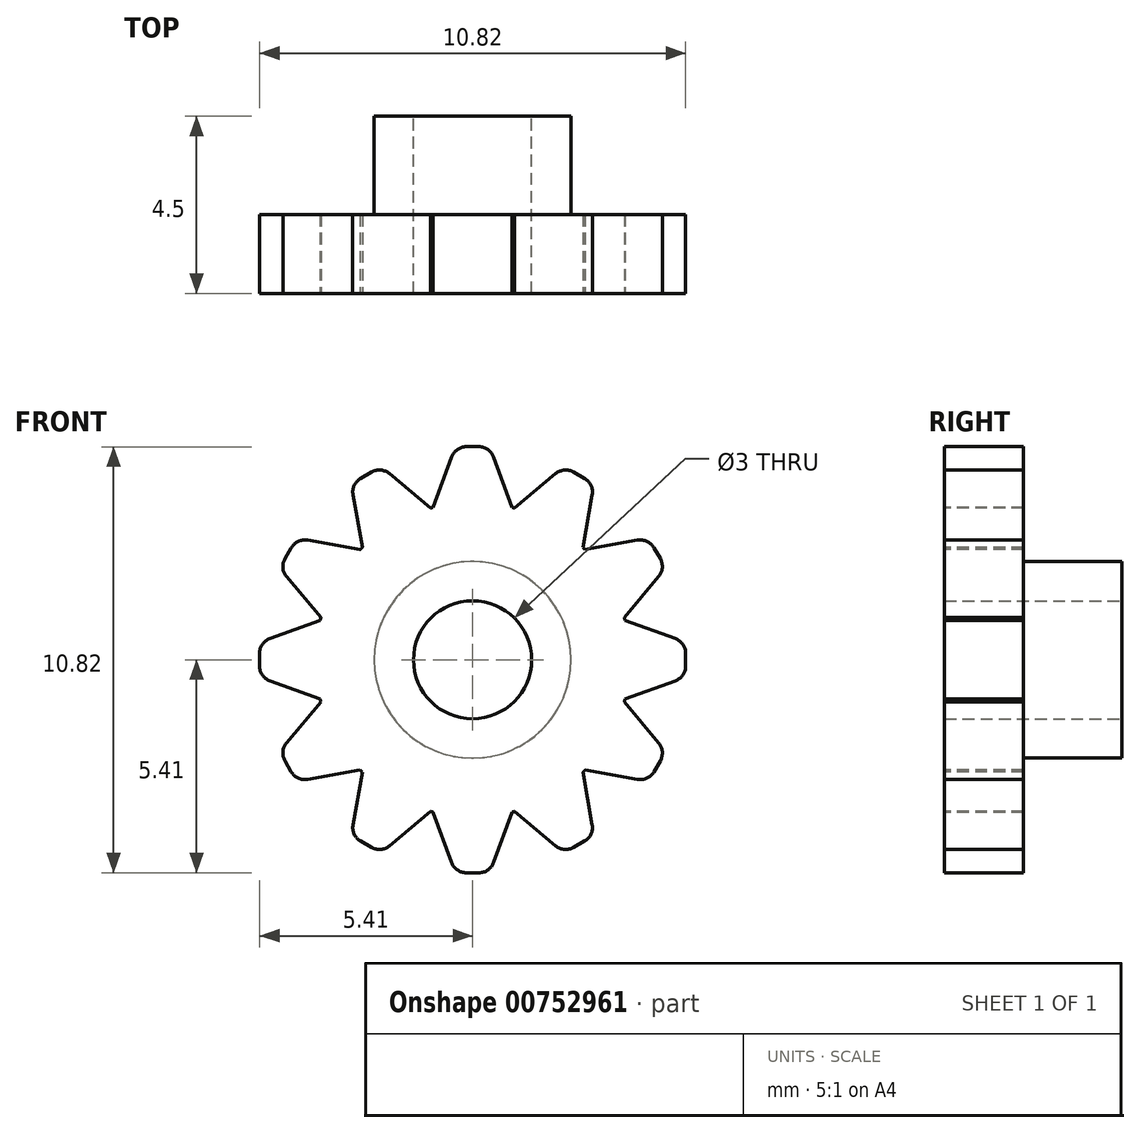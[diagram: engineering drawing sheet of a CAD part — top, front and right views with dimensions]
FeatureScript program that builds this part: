
annotation { "Feature Type Name" : "Feature", "Feature Type Description" : "" }
export const myFeature = defineFeature(function(context is Context, id is Id, definition is map)
    precondition{}
    {
        {
            var Q0;
            Q0=qCreatedBy(makeId("Front.planeOp"),FACE);
            var sketch = newSketch(context, id + "F0", { "sketchPlane" : qUnion([Q0])});
            skCircle(sketch, "E0", {"center": v(0, 0) * mm, "radius": 4 * mm});
            skCircle(sketch, "E1", {"center": v(0, 0) * mm, "radius": 1.5 * mm});
            skSolve(sketch);
        }
        {
            var Q0;
            Q0 = qSketchRegion(id + "F0", true);
            extrude(context, id + "F1", {"entities" : qUnion([Q0]), "depth" : 2 * mm, "offsetDistance" : 25 * mm});
        }
        {
            var Q0;
            Q0=makeQuery(id+"F1.opExtrude","CAP_FACE",FACE,{"disambiguationData":[OSD([sQuery(id+"F0.wireOp",EDGE,"E0")])],"isStart":false});
            var sketch = newSketch(context, id + "F2", { "sketchPlane" : qUnion([Q0])});
            skLineSegment(sketch, "E2", {"start": v(0, 0) * mm, "end": v(0, 7.76) * mm, "construction": true});
            skLineSegment(sketch, "E3", {"start": v(0, 5.41) * mm, "end": v(0.44, 5.41) * mm});
            skLineSegment(sketch, "E4", {"start": v(0.44, 5.41) * mm, "end": v(1, 3.87) * mm});
            skLineSegment(sketch, "E5.MirrorCS", {"start": v(0, 5.41) * mm, "end": v(-0.44, 5.41) * mm});
            skLineSegment(sketch, "E6.MirrorCS", {"start": v(-0.44, 5.41) * mm, "end": v(-1, 3.87) * mm});
            skLineSegment(sketch, "E7", {"start": v(-1, 3.87) * mm, "end": v(1, 3.87) * mm});
            skLineSegment(sketch, "E8.1.0", {"start": v(-2.8, 2.85) * mm, "end": v(-1.07, 3.85) * mm});
            skLineSegment(sketch, "E8.1.1", {"start": v(-3.09, 4.47) * mm, "end": v(-2.8, 2.85) * mm});
            skLineSegment(sketch, "E8.1.2", {"start": v(-2.33, 4.9) * mm, "end": v(-1.07, 3.85) * mm});
            skLineSegment(sketch, "E8.1.3", {"start": v(-2.7, 4.69) * mm, "end": v(-2.33, 4.9) * mm});
            skLineSegment(sketch, "E8.1.4", {"start": v(-2.7, 4.69) * mm, "end": v(-3.09, 4.47) * mm});
            skLineSegment(sketch, "E8.2.0", {"start": v(-3.85, 1.07) * mm, "end": v(-2.85, 2.8) * mm});
            skLineSegment(sketch, "E8.2.1", {"start": v(-4.9, 2.33) * mm, "end": v(-3.85, 1.07) * mm});
            skLineSegment(sketch, "E8.2.2", {"start": v(-4.47, 3.09) * mm, "end": v(-2.85, 2.8) * mm});
            skLineSegment(sketch, "E8.2.3", {"start": v(-4.69, 2.7) * mm, "end": v(-4.47, 3.09) * mm});
            skLineSegment(sketch, "E8.2.4", {"start": v(-4.69, 2.7) * mm, "end": v(-4.9, 2.33) * mm});
            skLineSegment(sketch, "E8.3.0", {"start": v(-3.87, -1) * mm, "end": v(-3.87, 1) * mm});
            skLineSegment(sketch, "E8.3.1", {"start": v(-5.41, -0.44) * mm, "end": v(-3.87, -1) * mm});
            skLineSegment(sketch, "E8.3.2", {"start": v(-5.41, 0.44) * mm, "end": v(-3.87, 1) * mm});
            skLineSegment(sketch, "E8.3.3", {"start": v(-5.41, 0) * mm, "end": v(-5.41, 0.44) * mm});
            skLineSegment(sketch, "E8.3.4", {"start": v(-5.41, 0) * mm, "end": v(-5.41, -0.44) * mm});
            skLineSegment(sketch, "E8.4.0", {"start": v(-2.85, -2.8) * mm, "end": v(-3.85, -1.07) * mm});
            skLineSegment(sketch, "E8.4.1", {"start": v(-4.47, -3.09) * mm, "end": v(-2.85, -2.8) * mm});
            skLineSegment(sketch, "E8.4.2", {"start": v(-4.9, -2.33) * mm, "end": v(-3.85, -1.07) * mm});
            skLineSegment(sketch, "E8.4.3", {"start": v(-4.69, -2.7) * mm, "end": v(-4.9, -2.33) * mm});
            skLineSegment(sketch, "E8.4.4", {"start": v(-4.69, -2.7) * mm, "end": v(-4.47, -3.09) * mm});
            skLineSegment(sketch, "E8.5.0", {"start": v(-1.07, -3.85) * mm, "end": v(-2.8, -2.85) * mm});
            skLineSegment(sketch, "E8.5.1", {"start": v(-2.33, -4.9) * mm, "end": v(-1.07, -3.85) * mm});
            skLineSegment(sketch, "E8.5.2", {"start": v(-3.09, -4.47) * mm, "end": v(-2.8, -2.85) * mm});
            skLineSegment(sketch, "E8.5.3", {"start": v(-2.7, -4.69) * mm, "end": v(-3.09, -4.47) * mm});
            skLineSegment(sketch, "E8.5.4", {"start": v(-2.7, -4.69) * mm, "end": v(-2.33, -4.9) * mm});
            skLineSegment(sketch, "E8.6.0", {"start": v(1, -3.87) * mm, "end": v(-1, -3.87) * mm});
            skLineSegment(sketch, "E8.6.1", {"start": v(0.44, -5.41) * mm, "end": v(1, -3.87) * mm});
            skLineSegment(sketch, "E8.6.2", {"start": v(-0.44, -5.41) * mm, "end": v(-1, -3.87) * mm});
            skLineSegment(sketch, "E8.6.3", {"start": v(0, -5.41) * mm, "end": v(-0.44, -5.41) * mm});
            skLineSegment(sketch, "E8.6.4", {"start": v(0, -5.41) * mm, "end": v(0.44, -5.41) * mm});
            skLineSegment(sketch, "E8.7.0", {"start": v(2.8, -2.85) * mm, "end": v(1.07, -3.85) * mm});
            skLineSegment(sketch, "E8.7.1", {"start": v(3.09, -4.47) * mm, "end": v(2.8, -2.85) * mm});
            skLineSegment(sketch, "E8.7.2", {"start": v(2.33, -4.9) * mm, "end": v(1.07, -3.85) * mm});
            skLineSegment(sketch, "E8.7.3", {"start": v(2.7, -4.69) * mm, "end": v(2.33, -4.9) * mm});
            skLineSegment(sketch, "E8.7.4", {"start": v(2.7, -4.69) * mm, "end": v(3.09, -4.47) * mm});
            skLineSegment(sketch, "E8.8.0", {"start": v(3.85, -1.07) * mm, "end": v(2.85, -2.8) * mm});
            skLineSegment(sketch, "E8.8.1", {"start": v(4.9, -2.33) * mm, "end": v(3.85, -1.07) * mm});
            skLineSegment(sketch, "E8.8.2", {"start": v(4.47, -3.09) * mm, "end": v(2.85, -2.8) * mm});
            skLineSegment(sketch, "E8.8.3", {"start": v(4.69, -2.7) * mm, "end": v(4.47, -3.09) * mm});
            skLineSegment(sketch, "E8.8.4", {"start": v(4.69, -2.7) * mm, "end": v(4.9, -2.33) * mm});
            skLineSegment(sketch, "E8.9.0", {"start": v(3.87, 1) * mm, "end": v(3.87, -1) * mm});
            skLineSegment(sketch, "E8.9.1", {"start": v(5.41, 0.44) * mm, "end": v(3.87, 1) * mm});
            skLineSegment(sketch, "E8.9.2", {"start": v(5.41, -0.44) * mm, "end": v(3.87, -1) * mm});
            skLineSegment(sketch, "E8.9.3", {"start": v(5.41, 0) * mm, "end": v(5.41, -0.44) * mm});
            skLineSegment(sketch, "E8.9.4", {"start": v(5.41, 0) * mm, "end": v(5.41, 0.44) * mm});
            skLineSegment(sketch, "E8.10.0", {"start": v(2.85, 2.8) * mm, "end": v(3.85, 1.07) * mm});
            skLineSegment(sketch, "E8.10.1", {"start": v(4.47, 3.09) * mm, "end": v(2.85, 2.8) * mm});
            skLineSegment(sketch, "E8.10.2", {"start": v(4.9, 2.33) * mm, "end": v(3.85, 1.07) * mm});
            skLineSegment(sketch, "E8.10.3", {"start": v(4.69, 2.7) * mm, "end": v(4.9, 2.33) * mm});
            skLineSegment(sketch, "E8.10.4", {"start": v(4.69, 2.7) * mm, "end": v(4.47, 3.09) * mm});
            skLineSegment(sketch, "E8.11.0", {"start": v(1.07, 3.85) * mm, "end": v(2.8, 2.85) * mm});
            skLineSegment(sketch, "E8.11.1", {"start": v(2.33, 4.9) * mm, "end": v(1.07, 3.85) * mm});
            skLineSegment(sketch, "E8.11.2", {"start": v(3.09, 4.47) * mm, "end": v(2.8, 2.85) * mm});
            skLineSegment(sketch, "E8.11.3", {"start": v(2.7, 4.69) * mm, "end": v(3.09, 4.47) * mm});
            skLineSegment(sketch, "E8.11.4", {"start": v(2.7, 4.69) * mm, "end": v(2.33, 4.9) * mm});
            skPoint(sketch, "E8.center", {"position": v(0, 0) * mm});
            skSolve(sketch);
        }
        {
            var Q0;
            Q0 = qSketchRegion(id + "F2", true);
            var Q1;
            Q1=makeQuery(id+"F1.opExtrude","CAP_FACE",FACE,{"disambiguationData":[OSD([sQuery(id+"F0.wireOp",EDGE,"E0"),sQuery(id+"F0.wireOp",EDGE,"E1")])],"isStart":true});
            extrude(context, id + "F3", {"entities" : qUnion([Q0]), "operationType" : NewBodyOperationType.ADD, "endBound" : BoundingType.UP_TO_SURFACE, "oppositeDirection" : true, "depth" : 2 * mm, "endBoundEntityFace" : qUnion([Q1]), "offsetDistance" : 25 * mm});
        }
        {
            var Q0;
            Q0=makeQuery(id+"F3.boolean.opBoolean","MERGE",FACE,{"derivedFrom":[makeQuery(id+"F1.opExtrude","CAP_FACE",FACE,{"disambiguationData":[OSD([sQuery(id+"F0.wireOp",EDGE,"E0"),sQuery(id+"F0.wireOp",EDGE,"E1")])],"isStart":true}),makeQuery(id+"F3.opExtrude","CAP_FACE",FACE,{"disambiguationData":[OSD([sQuery(id+"F2.wireOp",EDGE,"E3"),sQuery(id+"F2.wireOp",EDGE,"E4"),sQuery(id+"F2.wireOp",EDGE,"E5.MirrorCS"),sQuery(id+"F2.wireOp",EDGE,"E6.MirrorCS"),sQuery(id+"F2.wireOp",EDGE,"E7")])],"isStart":false}),makeQuery(id+"F3.opExtrude","CAP_FACE",FACE,{"disambiguationData":[OSD([sQuery(id+"F2.wireOp",EDGE,"E8.1.0"),sQuery(id+"F2.wireOp",EDGE,"E8.1.1"),sQuery(id+"F2.wireOp",EDGE,"E8.1.2"),sQuery(id+"F2.wireOp",EDGE,"E8.1.3"),sQuery(id+"F2.wireOp",EDGE,"E8.1.4")])],"isStart":false}),makeQuery(id+"F3.opExtrude","CAP_FACE",FACE,{"disambiguationData":[OSD([sQuery(id+"F2.wireOp",EDGE,"E8.2.0"),sQuery(id+"F2.wireOp",EDGE,"E8.2.1"),sQuery(id+"F2.wireOp",EDGE,"E8.2.2"),sQuery(id+"F2.wireOp",EDGE,"E8.2.3"),sQuery(id+"F2.wireOp",EDGE,"E8.2.4")])],"isStart":false}),makeQuery(id+"F3.opExtrude","CAP_FACE",FACE,{"disambiguationData":[OSD([sQuery(id+"F2.wireOp",EDGE,"E8.3.0"),sQuery(id+"F2.wireOp",EDGE,"E8.3.1"),sQuery(id+"F2.wireOp",EDGE,"E8.3.2"),sQuery(id+"F2.wireOp",EDGE,"E8.3.3"),sQuery(id+"F2.wireOp",EDGE,"E8.3.4")])],"isStart":false}),makeQuery(id+"F3.opExtrude","CAP_FACE",FACE,{"disambiguationData":[OSD([sQuery(id+"F2.wireOp",EDGE,"E8.4.0"),sQuery(id+"F2.wireOp",EDGE,"E8.4.1"),sQuery(id+"F2.wireOp",EDGE,"E8.4.2"),sQuery(id+"F2.wireOp",EDGE,"E8.4.3"),sQuery(id+"F2.wireOp",EDGE,"E8.4.4")])],"isStart":false}),makeQuery(id+"F3.opExtrude","CAP_FACE",FACE,{"disambiguationData":[OSD([sQuery(id+"F2.wireOp",EDGE,"E8.5.0"),sQuery(id+"F2.wireOp",EDGE,"E8.5.1"),sQuery(id+"F2.wireOp",EDGE,"E8.5.2"),sQuery(id+"F2.wireOp",EDGE,"E8.5.3"),sQuery(id+"F2.wireOp",EDGE,"E8.5.4")])],"isStart":false}),makeQuery(id+"F3.opExtrude","CAP_FACE",FACE,{"disambiguationData":[OSD([sQuery(id+"F2.wireOp",EDGE,"E8.6.0"),sQuery(id+"F2.wireOp",EDGE,"E8.6.1"),sQuery(id+"F2.wireOp",EDGE,"E8.6.2"),sQuery(id+"F2.wireOp",EDGE,"E8.6.3"),sQuery(id+"F2.wireOp",EDGE,"E8.6.4")])],"isStart":false}),makeQuery(id+"F3.opExtrude","CAP_FACE",FACE,{"disambiguationData":[OSD([sQuery(id+"F2.wireOp",EDGE,"E8.7.0"),sQuery(id+"F2.wireOp",EDGE,"E8.7.1"),sQuery(id+"F2.wireOp",EDGE,"E8.7.2"),sQuery(id+"F2.wireOp",EDGE,"E8.7.3"),sQuery(id+"F2.wireOp",EDGE,"E8.7.4")])],"isStart":false}),makeQuery(id+"F3.opExtrude","CAP_FACE",FACE,{"disambiguationData":[OSD([sQuery(id+"F2.wireOp",EDGE,"E8.8.0"),sQuery(id+"F2.wireOp",EDGE,"E8.8.1"),sQuery(id+"F2.wireOp",EDGE,"E8.8.2"),sQuery(id+"F2.wireOp",EDGE,"E8.8.3"),sQuery(id+"F2.wireOp",EDGE,"E8.8.4")])],"isStart":false}),makeQuery(id+"F3.opExtrude","CAP_FACE",FACE,{"disambiguationData":[OSD([sQuery(id+"F2.wireOp",EDGE,"E8.9.0"),sQuery(id+"F2.wireOp",EDGE,"E8.9.1"),sQuery(id+"F2.wireOp",EDGE,"E8.9.2"),sQuery(id+"F2.wireOp",EDGE,"E8.9.3"),sQuery(id+"F2.wireOp",EDGE,"E8.9.4")])],"isStart":false}),makeQuery(id+"F3.opExtrude","CAP_FACE",FACE,{"disambiguationData":[OSD([sQuery(id+"F2.wireOp",EDGE,"E8.10.0"),sQuery(id+"F2.wireOp",EDGE,"E8.10.1"),sQuery(id+"F2.wireOp",EDGE,"E8.10.2"),sQuery(id+"F2.wireOp",EDGE,"E8.10.3"),sQuery(id+"F2.wireOp",EDGE,"E8.10.4")])],"isStart":false}),makeQuery(id+"F3.opExtrude","CAP_FACE",FACE,{"disambiguationData":[OSD([sQuery(id+"F2.wireOp",EDGE,"E8.11.0"),sQuery(id+"F2.wireOp",EDGE,"E8.11.1"),sQuery(id+"F2.wireOp",EDGE,"E8.11.2"),sQuery(id+"F2.wireOp",EDGE,"E8.11.3"),sQuery(id+"F2.wireOp",EDGE,"E8.11.4")])],"isStart":false})]});
            var sketch = newSketch(context, id + "F4", { "sketchPlane" : qUnion([Q0])});
            skCircle(sketch, "E9.0", {"center": v(0, 0) * mm, "radius": 1.5 * mm});
            skCircle(sketch, "E10.0", {"center": v(0, 0) * mm, "radius": 2.5 * mm});
            skSolve(sketch);
        }
        {
            var Q0;
            Q0 = qSketchRegion(id + "F4", true);
            extrude(context, id + "F5", {"entities" : qUnion([Q0]), "operationType" : NewBodyOperationType.ADD, "depth" : 2.5 * mm, "offsetDistance" : 25 * mm});
        }
        {
            var Q0;
            Q0=makeQuery(id+"F3.opExtrude","SWEPT_EDGE",EDGE,{"disambiguationData":[OSD([sQuery(id+"F2.wireOp",EDGE,"E8.11.1"),sQuery(id+"F2.wireOp",EDGE,"E8.11.4")])]});
            var Q1;
            Q1=makeQuery(id+"F3.opExtrude","SWEPT_EDGE",EDGE,{"disambiguationData":[OSD([sQuery(id+"F2.wireOp",EDGE,"E8.11.2"),sQuery(id+"F2.wireOp",EDGE,"E8.11.3")])]});
            var Q2;
            Q2=makeQuery(id+"F3.opExtrude","SWEPT_EDGE",EDGE,{"disambiguationData":[OSD([sQuery(id+"F2.wireOp",EDGE,"E8.10.1"),sQuery(id+"F2.wireOp",EDGE,"E8.10.4")])]});
            var Q3;
            Q3=makeQuery(id+"F3.opExtrude","SWEPT_EDGE",EDGE,{"disambiguationData":[OSD([sQuery(id+"F2.wireOp",EDGE,"E8.10.2"),sQuery(id+"F2.wireOp",EDGE,"E8.10.3")])]});
            var Q4;
            Q4=makeQuery(id+"F3.opExtrude","SWEPT_EDGE",EDGE,{"disambiguationData":[OSD([sQuery(id+"F2.wireOp",EDGE,"E8.9.1"),sQuery(id+"F2.wireOp",EDGE,"E8.9.4")])]});
            var Q5;
            Q5=makeQuery(id+"F3.opExtrude","SWEPT_EDGE",EDGE,{"disambiguationData":[OSD([sQuery(id+"F2.wireOp",EDGE,"E8.9.2"),sQuery(id+"F2.wireOp",EDGE,"E8.9.3")])]});
            var Q6;
            Q6=makeQuery(id+"F3.opExtrude","SWEPT_EDGE",EDGE,{"disambiguationData":[OSD([sQuery(id+"F2.wireOp",EDGE,"E8.8.1"),sQuery(id+"F2.wireOp",EDGE,"E8.8.4")])]});
            var Q7;
            Q7=makeQuery(id+"F3.opExtrude","SWEPT_EDGE",EDGE,{"disambiguationData":[OSD([sQuery(id+"F2.wireOp",EDGE,"E8.8.2"),sQuery(id+"F2.wireOp",EDGE,"E8.8.3")])]});
            var Q8;
            Q8=makeQuery(id+"F3.opExtrude","SWEPT_EDGE",EDGE,{"disambiguationData":[OSD([sQuery(id+"F2.wireOp",EDGE,"E8.7.1"),sQuery(id+"F2.wireOp",EDGE,"E8.7.4")])]});
            var Q9;
            Q9=makeQuery(id+"F3.opExtrude","SWEPT_EDGE",EDGE,{"disambiguationData":[OSD([sQuery(id+"F2.wireOp",EDGE,"E8.7.2"),sQuery(id+"F2.wireOp",EDGE,"E8.7.3")])]});
            var Q10;
            Q10=makeQuery(id+"F3.opExtrude","SWEPT_EDGE",EDGE,{"disambiguationData":[OSD([sQuery(id+"F2.wireOp",EDGE,"E8.6.1"),sQuery(id+"F2.wireOp",EDGE,"E8.6.4")])]});
            var Q11;
            Q11=makeQuery(id+"F3.opExtrude","SWEPT_EDGE",EDGE,{"disambiguationData":[OSD([sQuery(id+"F2.wireOp",EDGE,"E8.6.2"),sQuery(id+"F2.wireOp",EDGE,"E8.6.3")])]});
            var Q12;
            Q12=makeQuery(id+"F3.opExtrude","SWEPT_EDGE",EDGE,{"disambiguationData":[OSD([sQuery(id+"F2.wireOp",EDGE,"E8.5.1"),sQuery(id+"F2.wireOp",EDGE,"E8.5.4")])]});
            var Q13;
            Q13=makeQuery(id+"F3.opExtrude","SWEPT_EDGE",EDGE,{"disambiguationData":[OSD([sQuery(id+"F2.wireOp",EDGE,"E8.5.2"),sQuery(id+"F2.wireOp",EDGE,"E8.5.3")])]});
            var Q14;
            Q14=makeQuery(id+"F3.opExtrude","SWEPT_EDGE",EDGE,{"disambiguationData":[OSD([sQuery(id+"F2.wireOp",EDGE,"E8.4.1"),sQuery(id+"F2.wireOp",EDGE,"E8.4.4")])]});
            var Q15;
            Q15=makeQuery(id+"F3.opExtrude","SWEPT_EDGE",EDGE,{"disambiguationData":[OSD([sQuery(id+"F2.wireOp",EDGE,"E8.4.2"),sQuery(id+"F2.wireOp",EDGE,"E8.4.3")])]});
            var Q16;
            Q16=makeQuery(id+"F3.opExtrude","SWEPT_EDGE",EDGE,{"disambiguationData":[OSD([sQuery(id+"F2.wireOp",EDGE,"E8.3.1"),sQuery(id+"F2.wireOp",EDGE,"E8.3.4")])]});
            var Q17;
            Q17=makeQuery(id+"F3.opExtrude","SWEPT_EDGE",EDGE,{"disambiguationData":[OSD([sQuery(id+"F2.wireOp",EDGE,"E8.3.2"),sQuery(id+"F2.wireOp",EDGE,"E8.3.3")])]});
            var Q18;
            Q18=makeQuery(id+"F3.opExtrude","SWEPT_EDGE",EDGE,{"disambiguationData":[OSD([sQuery(id+"F2.wireOp",EDGE,"E8.2.1"),sQuery(id+"F2.wireOp",EDGE,"E8.2.4")])]});
            var Q19;
            Q19=makeQuery(id+"F3.opExtrude","SWEPT_EDGE",EDGE,{"disambiguationData":[OSD([sQuery(id+"F2.wireOp",EDGE,"E8.2.2"),sQuery(id+"F2.wireOp",EDGE,"E8.2.3")])]});
            var Q20;
            Q20=makeQuery(id+"F3.opExtrude","SWEPT_EDGE",EDGE,{"disambiguationData":[OSD([sQuery(id+"F2.wireOp",EDGE,"E8.1.1"),sQuery(id+"F2.wireOp",EDGE,"E8.1.4")])]});
            var Q21;
            Q21=makeQuery(id+"F3.opExtrude","SWEPT_EDGE",EDGE,{"disambiguationData":[OSD([sQuery(id+"F2.wireOp",EDGE,"E8.1.2"),sQuery(id+"F2.wireOp",EDGE,"E8.1.3")])]});
            var Q22;
            Q22=makeQuery(id+"F3.opExtrude","SWEPT_EDGE",EDGE,{"disambiguationData":[OSD([sQuery(id+"F2.wireOp",EDGE,"E5.MirrorCS"),sQuery(id+"F2.wireOp",EDGE,"E6.MirrorCS")])]});
            var Q23;
            Q23=makeQuery(id+"F3.opExtrude","SWEPT_EDGE",EDGE,{"disambiguationData":[OSD([sQuery(id+"F2.wireOp",EDGE,"E3"),sQuery(id+"F2.wireOp",EDGE,"E4")])]});
            fillet(context, id + "F6", {"entities" : qUnion([Q0, Q1, Q2, Q3, Q4, Q5, Q6, Q7, Q8, Q9, Q10, Q11, Q12, Q13, Q14, Q15, Q16, Q17, Q18, Q19, Q20, Q21, Q22, Q23]), "radius" : 0.4 * mm, "tangentPropagation" : true, "allowEdgeOverflow" : false});
        }
    });
